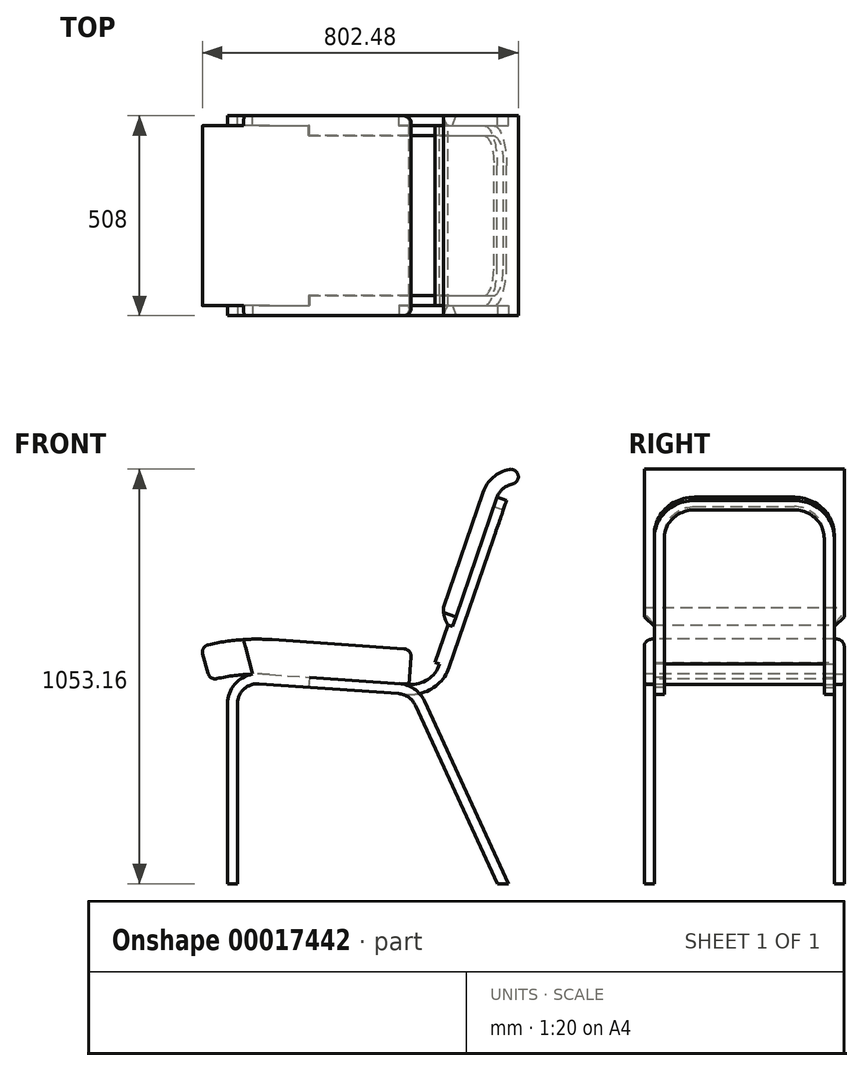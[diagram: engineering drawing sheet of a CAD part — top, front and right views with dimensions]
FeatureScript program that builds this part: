
annotation { "Feature Type Name" : "Feature", "Feature Type Description" : "" }
export const myFeature = defineFeature(function(context is Context, id is Id, definition is map)
    precondition{}
    {
        {
            var Q0;
            Q0=qCreatedBy(makeId("Front.planeOp"),FACE);
            cPlane(context, id + "F0", {"entities" : qUnion([Q0]), "cplaneType" : CPlaneType.OFFSET, "offset" : 254 * mm, "oppositeDirection" : true, "width" : 152.4 * mm, "height" : 152.4 * mm});
        }
        {
            var Q0;
            Q0=qCreatedBy(makeId("Front.planeOp"),FACE);
            var sketch = newSketch(context, id + "F1", { "sketchPlane" : qUnion([Q0])});
            skLineSegment(sketch, "E0", {"start": v(0, 0) * mm, "end": v(0, 457.2) * mm});
            skLineSegment(sketch, "E1", {"start": v(54.34, 507.88) * mm, "end": v(409.08, 483.07) * mm});
            skLineSegment(sketch, "E2", {"start": v(451.68, 453.63) * mm, "end": v(660.4, 0) * mm});
            skPoint(sketch, "E3.visualSharp", {"position": v(0, 511.68) * mm});
            skArc(sketch, "E3.filletArc", {"start": v(54.34, 507.88) * mm, "mid": v(16.15, 494.35) * mm, "end": v(0, 457.2) * mm});
            skPoint(sketch, "E4.visualSharp", {"position": v(439.1, 480.97) * mm});
            skArc(sketch, "E4.filletArc", {"start": v(451.68, 453.63) * mm, "mid": v(434.41, 474.19) * mm, "end": v(409.08, 483.07) * mm});
            skLineSegment(sketch, "E5.0", {"start": v(474.76, 464.25) * mm, "end": v(688.36, 0) * mm});
            skArc(sketch, "E5.1", {"start": v(474.76, 464.25) * mm, "mid": v(448.85, 495.08) * mm, "end": v(410.85, 508.4) * mm});
            skLineSegment(sketch, "E5.2", {"start": v(56.12, 533.21) * mm, "end": v(410.85, 508.4) * mm});
            skArc(sketch, "E5.3", {"start": v(56.12, 533.21) * mm, "mid": v(-1.17, 512.93) * mm, "end": v(-25.4, 457.2) * mm});
            skLineSegment(sketch, "E5.4", {"start": v(-25.4, 0) * mm, "end": v(-25.4, 457.2) * mm});
            skLineSegment(sketch, "E6", {"start": v(660.4, 0) * mm, "end": v(688.36, 0) * mm});
            skLineSegment(sketch, "E7", {"start": v(-25.4, 0) * mm, "end": v(0, 0) * mm});
            skSolve(sketch);
        }
        {
            var Q0;
            Q0=makeQuery(id+"F1.imprint","IMPRINT",FACE,{"disambiguationData":[TD([[makeQuery(id+"F1.imprint","IMPRINT",EDGE,{"derivedFrom":sQuery(id+"F1.wireOp",EDGE,"E0")}),1.0]])]});
            extrude(context, id + "F2", {"entities" : qUnion([Q0]), "oppositeDirection" : true, "depth" : 25.4 * mm});
        }
        {
            var Q0;
            Q0=makeQuery(id+"F2.opExtrude","CAP_FACE",FACE,{"disambiguationData":[OSD([sQuery(id+"F1.wireOp",EDGE,"E0"),sQuery(id+"F1.wireOp",EDGE,"E1"),sQuery(id+"F1.wireOp",EDGE,"E2"),sQuery(id+"F1.wireOp",EDGE,"E3.filletArc"),sQuery(id+"F1.wireOp",EDGE,"E4.filletArc"),sQuery(id+"F1.wireOp",EDGE,"E5.0"),sQuery(id+"F1.wireOp",EDGE,"E5.1"),sQuery(id+"F1.wireOp",EDGE,"E5.2"),sQuery(id+"F1.wireOp",EDGE,"E5.3"),sQuery(id+"F1.wireOp",EDGE,"E5.4"),sQuery(id+"F1.wireOp",EDGE,"E6"),sQuery(id+"F1.wireOp",EDGE,"E7")])],"isStart":false});
            var sketch = newSketch(context, id + "F3", { "sketchPlane" : qUnion([Q0])});
            skArc(sketch, "E8", {"start": v(-436.19, 506.64) * mm, "mid": v(-483.56, 519.1) * mm, "end": v(-513.55, 557.84) * mm});
            skArc(sketch, "E9.0", {"start": v(-434.42, 481.3) * mm, "mid": v(-497.58, 497.93) * mm, "end": v(-537.57, 549.57) * mm});
            skLineSegment(sketch, "E10", {"start": v(-513.55, 557.84) * mm, "end": v(-537.57, 549.57) * mm});
            skLineSegment(sketch, "E11", {"start": v(-436.19, 506.64) * mm, "end": v(-182.8, 524.36) * mm});
            skLineSegment(sketch, "E12", {"start": v(-182.8, 524.36) * mm, "end": v(-181.03, 499.02) * mm});
            skLineSegment(sketch, "E13", {"start": v(-181.03, 499.02) * mm, "end": v(-434.42, 481.3) * mm});
            skLineSegment(sketch, "E14", {"start": v(-441.5, 582.65) * mm, "end": v(-434.42, 481.3) * mm, "construction": true});
            skLineSegment(sketch, "E15", {"start": v(-441.5, 582.65) * mm, "end": v(-537.57, 549.57) * mm, "construction": true});
            skLineSegment(sketch, "E16.0", {"start": v(-56.12, 533.21) * mm, "end": v(-410.85, 508.4) * mm, "construction": true});
            skSolve(sketch);
        }
        {
            var Q0;
            Q0 = qSketchRegion(id + "F3", true);
            extrude(context, id + "F4", {"entities" : qUnion([Q0]), "operationType" : NewBodyOperationType.ADD, "depth" : 25.4 * mm});
        }
        {
            var Q0;
            Q0=makeQuery(id+"F4.opExtrude","SWEPT_EDGE",EDGE,{"disambiguationData":[OSD([sQuery(id+"F3.wireOp",EDGE,"E9.0"),sQuery(id+"F3.wireOp",EDGE,"E10")])]});
            cPlane(context, id + "F5", {"entities" : qUnion([Q0]), "cplaneType" : CPlaneType.LINE_ANGLE, "offset" : 152.4 * mm, "angle" : 71 * degree, "width" : 152.4 * mm, "height" : 152.4 * mm});
        }
        {
            var Q0;
            Q0=qCreatedBy(id+"F5.planeOp",FACE);
            var sketch = newSketch(context, id + "F6", { "sketchPlane" : qUnion([Q0])});
            skLineSegment(sketch, "E17", {"start": v(25.4, 694.65) * mm, "end": v(25.4, 1041.73) * mm});
            skLineSegment(sketch, "E18", {"start": v(127, 1143.33) * mm, "end": v(254, 1143.33) * mm});
            skPoint(sketch, "E19.visualSharp", {"position": v(25.4, 1143.33) * mm});
            skArc(sketch, "E19.filletArc", {"start": v(127, 1143.33) * mm, "mid": v(55.16, 1113.57) * mm, "end": v(25.4, 1041.73) * mm});
            skSolve(sketch);
        }
        {
            var Q0;
            Q0=makeQuery(id+"F4.opExtrude","SWEPT_FACE",FACE,{"disambiguationData":[OSD([sQuery(id+"F3.wireOp",EDGE,"E10")])]});
            var Q1;
            Q1 = qConstructionFilter(qBodyType(qCreatedBy(id + "F6" ,EDGE), BodyType.WIRE), ConstructionObject.NO);
            sweep(context, id + "F7", {"operationType" : NewBodyOperationType.ADD, "profiles" : qUnion([Q0]), "path" : qUnion([Q1])});
        }
        {
            var Q0;
            Q0=makeQuery(id+"F4.opExtrude","SWEPT_EDGE",EDGE,{"disambiguationData":[OSD([sQuery(id+"F3.wireOp",EDGE,"E8"),sQuery(id+"F3.wireOp",EDGE,"E11")])]});
            cPlane(context, id + "F8", {"entities" : qUnion([Q0]), "cplaneType" : CPlaneType.LINE_ANGLE, "offset" : 152.4 * mm, "angle" : 86 * degree, "width" : 152.4 * mm, "height" : 152.4 * mm});
        }
        {
            var Q0;
            Q0=qCreatedBy(id+"F8.planeOp",FACE);
            var sketch = newSketch(context, id + "F9", { "sketchPlane" : qUnion([Q0])});
            skLineSegment(sketch, "E20.bottom", {"start": v(0, 535.83) * mm, "end": v(254, 535.83) * mm});
            skLineSegment(sketch, "E20.top", {"start": v(0, 624.73) * mm, "end": v(254, 624.73) * mm});
            skLineSegment(sketch, "E20.left", {"start": v(0, 535.83) * mm, "end": v(0, 624.73) * mm});
            skLineSegment(sketch, "E20.right", {"start": v(254, 535.83) * mm, "end": v(254, 624.73) * mm});
            skSolve(sketch);
        }
        {
            var Q0;
            Q0=qCreatedBy(makeId("Front.planeOp"),FACE);
            var sketch = newSketch(context, id + "F10", { "sketchPlane" : qUnion([Q0])});
            skLineSegment(sketch, "E21", {"start": v(436.19, 506.64) * mm, "end": v(81.45, 531.44) * mm});
            skArc(sketch, "E22", {"start": v(81.45, 531.44) * mm, "mid": v(5, 530.38) * mm, "end": v(-70.22, 516.59) * mm});
            skSolve(sketch);
        }
        {
            var Q0;
            Q0 = qSketchRegion(id + "F9", true);
            var Q1;
            Q1 = qConstructionFilter(qBodyType(qCreatedBy(id + "F10" ,EDGE), BodyType.WIRE), ConstructionObject.NO);
            sweep(context, id + "F11", {"operationType" : NewBodyOperationType.ADD, "profiles" : qUnion([Q0]), "path" : qUnion([Q1])});
        }
        {
            var Q0;
            Q0=qCreatedBy(id+"F0.planeOp",FACE);
            var sketch = newSketch(context, id + "F12", { "sketchPlane" : qUnion([Q0])});
            skLineSegment(sketch, "E23.0", {"start": v(513.55, 557.84) * mm, "end": v(626.55, 886.02) * mm});
            skLineSegment(sketch, "E24", {"start": v(513.55, 557.84) * mm, "end": v(501.54, 561.98) * mm});
            skLineSegment(sketch, "E25", {"start": v(501.54, 561.98) * mm, "end": v(534.62, 658.04) * mm});
            skLineSegment(sketch, "E26", {"start": v(523, 702.34) * mm, "end": v(623.6, 994.49) * mm});
            skLineSegment(sketch, "E27.0", {"start": v(626.55, 886.02) * mm, "end": v(659.63, 982.08) * mm});
            skLineSegment(sketch, "E28", {"start": v(513.55, 557.84) * mm, "end": v(659.63, 982.08) * mm, "construction": true});
            skArc(sketch, "E29", {"start": v(659.63, 982.08) * mm, "mid": v(674.33, 1003.88) * mm, "end": v(697.97, 1015.41) * mm});
            skArc(sketch, "E30.0", {"start": v(623.6, 994.49) * mm, "mid": v(649.34, 1032.64) * mm, "end": v(690.7, 1052.81) * mm});
            skLineSegment(sketch, "E31", {"start": v(713.02, 1037.83) * mm, "end": v(713.02, 1037.83) * mm});
            skPoint(sketch, "E32.visualSharp", {"position": v(717.48, 1015.39) * mm});
            skArc(sketch, "E32.filletArc", {"start": v(697.97, 1015.41) * mm, "mid": v(710.15, 1023.5) * mm, "end": v(713.02, 1037.83) * mm});
            skPoint(sketch, "E33.visualSharp", {"position": v(709.71, 1054.42) * mm});
            skArc(sketch, "E33.filletArc", {"start": v(713.02, 1037.83) * mm, "mid": v(704.95, 1049.93) * mm, "end": v(690.7, 1052.81) * mm});
            skLineSegment(sketch, "E34", {"start": v(697.97, 1015.41) * mm, "end": v(707.66, 965.54) * mm, "construction": true});
            skLineSegment(sketch, "E35", {"start": v(659.63, 982.08) * mm, "end": v(707.66, 965.54) * mm, "construction": true});
            skArc(sketch, "E36", {"start": v(523, 702.34) * mm, "mid": v(525.4, 679.3) * mm, "end": v(534.62, 658.04) * mm});
            skSolve(sketch);
        }
        {
            var Q0;
            Q0 = qSketchRegion(id + "F12", true);
            var Q1;
            Q1=makeQuery(id+"F11.boolean.opBoolean","MERGE",FACE,{"derivedFrom":[makeQuery(id+"F2.opExtrude","CAP_FACE",FACE,{"disambiguationData":[OSD([sQuery(id+"F1.wireOp",EDGE,"E0"),sQuery(id+"F1.wireOp",EDGE,"E1"),sQuery(id+"F1.wireOp",EDGE,"E2"),sQuery(id+"F1.wireOp",EDGE,"E3.filletArc"),sQuery(id+"F1.wireOp",EDGE,"E4.filletArc"),sQuery(id+"F1.wireOp",EDGE,"E5.0"),sQuery(id+"F1.wireOp",EDGE,"E5.1"),sQuery(id+"F1.wireOp",EDGE,"E5.2"),sQuery(id+"F1.wireOp",EDGE,"E5.3"),sQuery(id+"F1.wireOp",EDGE,"E5.4"),sQuery(id+"F1.wireOp",EDGE,"E6"),sQuery(id+"F1.wireOp",EDGE,"E7")])],"isStart":true}),makeQuery(id+"F11.opSweep","SWEPT_FACE",FACE,{"disambiguationData":[OSD([sQuery(id+"F9.wireOp",EDGE,"E20.left"),sQuery(id+"F10.wireOp",EDGE,"E21")])]})]});
            extrude(context, id + "F13", {"entities" : qUnion([Q0]), "operationType" : NewBodyOperationType.ADD, "endBound" : BoundingType.UP_TO_SURFACE, "endBoundEntityFace" : qUnion([Q1]), "depth" : 30.48 * mm});
        }
        {
            var Q0;
            Q0=makeQuery(id+"F13.boolean.opBoolean","SPLIT",FACE,{"disambiguationData":[TD([makeQuery(id+"F13.opExtrude","SWEPT_FACE",FACE,{"disambiguationData":[OSD([sQuery(id+"F12.wireOp",EDGE,"E29")])]})])],"derivedFrom":makeQuery(id+"F13.opExtrude","SWEPT_FACE",FACE,{"disambiguationData":[OSD([sQuery(id+"F12.wireOp",EDGE,"E23.0"),sQuery(id+"F12.wireOp",EDGE,"E27.0")])]})});
            var sketch = newSketch(context, id + "F14", { "sketchPlane" : qUnion([Q0])});
            skLineSegment(sketch, "E37", {"start": v(25.4, 694.65) * mm, "end": v(25.4, 796.25) * mm});
            skLineSegment(sketch, "E38", {"start": v(25.4, 796.25) * mm, "end": v(0, 821.65) * mm});
            skLineSegment(sketch, "E39", {"start": v(0, 821.65) * mm, "end": v(0, 694.65) * mm});
            skLineSegment(sketch, "E40", {"start": v(0, 694.65) * mm, "end": v(25.4, 694.65) * mm});
            skSolve(sketch);
        }
        {
            var Q0;
            Q0 = qSketchRegion(id + "F14", true);
            extrude(context, id + "F15", {"entities" : qUnion([Q0]), "operationType" : NewBodyOperationType.REMOVE, "endBound" : BoundingType.UP_TO_NEXT, "oppositeDirection" : true, "depth" : 30.48 * mm});
        }
        {
            var Q0;
            Q0=makeQuery(id+"F11.boolean.opBoolean","MERGE",FACE,{"derivedFrom":[makeQuery(id+"F2.opExtrude","CAP_FACE",FACE,{"disambiguationData":[OSD([sQuery(id+"F1.wireOp",EDGE,"E0"),sQuery(id+"F1.wireOp",EDGE,"E1"),sQuery(id+"F1.wireOp",EDGE,"E2"),sQuery(id+"F1.wireOp",EDGE,"E3.filletArc"),sQuery(id+"F1.wireOp",EDGE,"E4.filletArc"),sQuery(id+"F1.wireOp",EDGE,"E5.0"),sQuery(id+"F1.wireOp",EDGE,"E5.1"),sQuery(id+"F1.wireOp",EDGE,"E5.2"),sQuery(id+"F1.wireOp",EDGE,"E5.3"),sQuery(id+"F1.wireOp",EDGE,"E5.4"),sQuery(id+"F1.wireOp",EDGE,"E6"),sQuery(id+"F1.wireOp",EDGE,"E7")])],"isStart":true}),makeQuery(id+"F11.opSweep","SWEPT_FACE",FACE,{"disambiguationData":[OSD([sQuery(id+"F9.wireOp",EDGE,"E20.left"),sQuery(id+"F10.wireOp",EDGE,"E21")])]})]});
            var sketch = newSketch(context, id + "F16", { "sketchPlane" : qUnion([Q0])});
            skArc(sketch, "E41.0", {"start": v(14.79, 620.35) * mm, "mid": v(-39.81, 614.1) * mm, "end": v(-93.51, 602.38) * mm});
            skLineSegment(sketch, "E41.1", {"start": v(-93.51, 602.38) * mm, "end": v(-70.22, 516.59) * mm});
            skArc(sketch, "E41.2", {"start": v(38.66, 532.43) * mm, "mid": v(-16.26, 527.8) * mm, "end": v(-70.22, 516.59) * mm});
            skLineSegment(sketch, "E42", {"start": v(38.66, 532.43) * mm, "end": v(14.79, 620.35) * mm});
            skPoint(sketch, "E43.orphan", {"position": v(87.65, 620.13) * mm});
            skSolve(sketch);
        }
        {
            var Q0;
            Q0 = qSketchRegion(id + "F16", true);
            extrude(context, id + "F17", {"entities" : qUnion([Q0]), "operationType" : NewBodyOperationType.REMOVE, "oppositeDirection" : true, "depth" : 25.4 * mm});
        }
        {
            var Q0;
            Q0=makeQuery(id+"F2.opExtrude","SWEPT_BODY",BODY,{"disambiguationData":[OSD([sQuery(id+"F1.wireOp",EDGE,"E0"),sQuery(id+"F1.wireOp",EDGE,"E1"),sQuery(id+"F1.wireOp",EDGE,"E2"),sQuery(id+"F1.wireOp",EDGE,"E3.filletArc"),sQuery(id+"F1.wireOp",EDGE,"E4.filletArc"),sQuery(id+"F1.wireOp",EDGE,"E5.0"),sQuery(id+"F1.wireOp",EDGE,"E5.1"),sQuery(id+"F1.wireOp",EDGE,"E5.2"),sQuery(id+"F1.wireOp",EDGE,"E5.3"),sQuery(id+"F1.wireOp",EDGE,"E5.4"),sQuery(id+"F1.wireOp",EDGE,"E6"),sQuery(id+"F1.wireOp",EDGE,"E7")])]});
            var Q1;
            Q1=qCreatedBy(id+"F0.planeOp",FACE);
            mirror(context, id + "F18", {"operationType" : NewBodyOperationType.ADD, "entities" : qUnion([Q0]), "mirrorPlane" : qUnion([Q1])});
        }
        {
            var Q0;
            {var subQ0=makeQuery(id+"F11.opSweep","CAP_EDGE",EDGE,{"disambiguationData":[OSD([sQuery(id+"F9.wireOp",EDGE,"E20.top"),sQuery(id+"F10.wireOp",VERTEX,"E22.end")])],"isStart":false});Q0=makeQuery(id+"F18.boolean.opBoolean","MERGE",EDGE,{"derivedFrom":[subQ0,makeQuery(id+"F18.opPattern","COPY",EDGE,{"derivedFrom":subQ0,"instanceName":"1"})]});}
            var Q1;
            Q1=makeQuery(id+"F17.boolean.opBoolean","COPY",EDGE,{"derivedFrom":makeQuery(id+"F17.opExtrude","CAP_EDGE",EDGE,{"disambiguationData":[OSD([sQuery(id+"F16.wireOp",EDGE,"E41.0")])],"isStart":false})});
            var Q2;
            Q2=makeQuery(id+"F17.boolean.opBoolean","COPY",EDGE,{"derivedFrom":makeQuery(id+"F17.opExtrude","SWEPT_EDGE",EDGE,{"disambiguationData":[OSD([sQuery(id+"F9.wireOp",EDGE,"E20.top"),sQuery(id+"F9.wireOp",EDGE,"E20.left"),sQuery(id+"F10.wireOp",EDGE,"E22"),sQuery(id+"F16.wireOp",EDGE,"E41.0"),sQuery(id+"F16.wireOp",EDGE,"E42")])]})});
            var Q3;
            {var subQ0=makeQuery(id+"F11.opSweep","CAP_EDGE",EDGE,{"disambiguationData":[OSD([sQuery(id+"F9.wireOp",EDGE,"E20.bottom"),sQuery(id+"F10.wireOp",VERTEX,"E22.end")])],"isStart":false});Q3=makeQuery(id+"F18.boolean.opBoolean","MERGE",EDGE,{"derivedFrom":[subQ0,makeQuery(id+"F18.opPattern","COPY",EDGE,{"derivedFrom":subQ0,"instanceName":"1"})]});}
            var Q4;
            Q4=makeQuery(id+"F17.boolean.opBoolean","COPY",EDGE,{"derivedFrom":makeQuery(id+"F17.opExtrude","CAP_EDGE",EDGE,{"disambiguationData":[OSD([sQuery(id+"F16.wireOp",EDGE,"E41.2")])],"isStart":false})});
            var Q5;
            Q5=makeQuery(id+"F17.boolean.opBoolean","COPY",EDGE,{"derivedFrom":makeQuery(id+"F17.opExtrude","CAP_EDGE",EDGE,{"disambiguationData":[OSD([sQuery(id+"F16.wireOp",EDGE,"E41.1")])],"isStart":false})});
            var Q6;
            Q6=makeQuery(id+"F17.boolean.opBoolean","COPY",EDGE,{"derivedFrom":makeQuery(id+"F17.opExtrude","CAP_EDGE",EDGE,{"disambiguationData":[OSD([sQuery(id+"F16.wireOp",EDGE,"E42")])],"isStart":true})});
            var Q7;
            Q7=makeQuery(id+"F11.opSweep","SWEPT_EDGE",EDGE,{"disambiguationData":[OSD([sQuery(id+"F9.wireOp",EDGE,"E20.top"),sQuery(id+"F9.wireOp",EDGE,"E20.left"),sQuery(id+"F10.wireOp",EDGE,"E22")])]});
            var Q8;
            Q8=makeQuery(id+"F11.opSweep","SWEPT_EDGE",EDGE,{"disambiguationData":[OSD([sQuery(id+"F9.wireOp",EDGE,"E20.top"),sQuery(id+"F9.wireOp",EDGE,"E20.left"),sQuery(id+"F10.wireOp",EDGE,"E21")])]});
            var Q9;
            {var subQ0=makeQuery(id+"F11.opSweep","CAP_EDGE",EDGE,{"disambiguationData":[OSD([sQuery(id+"F9.wireOp",EDGE,"E20.top"),sQuery(id+"F10.wireOp",VERTEX,"E21.start")])],"isStart":true});Q9=makeQuery(id+"F18.boolean.opBoolean","MERGE",EDGE,{"derivedFrom":[subQ0,makeQuery(id+"F18.opPattern","COPY",EDGE,{"derivedFrom":subQ0,"instanceName":"1"})]});}
            var Q10;
            Q10=makeQuery(id+"F11.opSweep","CAP_EDGE",EDGE,{"disambiguationData":[OSD([sQuery(id+"F9.wireOp",EDGE,"E20.left"),sQuery(id+"F10.wireOp",VERTEX,"E21.start")])],"isStart":true});
            var Q11;
            Q11=makeQuery(id+"F18.opPattern","COPY",EDGE,{"derivedFrom":makeQuery(id+"F17.boolean.opBoolean","COPY",EDGE,{"derivedFrom":makeQuery(id+"F17.opExtrude","CAP_EDGE",EDGE,{"disambiguationData":[OSD([sQuery(id+"F16.wireOp",EDGE,"E41.0")])],"isStart":false})}),"instanceName":"1"});
            var Q12;
            Q12=makeQuery(id+"F18.opPattern","COPY",EDGE,{"derivedFrom":makeQuery(id+"F11.opSweep","SWEPT_EDGE",EDGE,{"disambiguationData":[OSD([sQuery(id+"F9.wireOp",EDGE,"E20.top"),sQuery(id+"F9.wireOp",EDGE,"E20.left"),sQuery(id+"F10.wireOp",EDGE,"E22")])]}),"instanceName":"1"});
            var Q13;
            Q13=makeQuery(id+"F18.opPattern","COPY",EDGE,{"derivedFrom":makeQuery(id+"F11.opSweep","SWEPT_EDGE",EDGE,{"disambiguationData":[OSD([sQuery(id+"F9.wireOp",EDGE,"E20.top"),sQuery(id+"F9.wireOp",EDGE,"E20.left"),sQuery(id+"F10.wireOp",EDGE,"E21")])]}),"instanceName":"1"});
            var Q14;
            Q14=makeQuery(id+"F18.opPattern","COPY",EDGE,{"derivedFrom":makeQuery(id+"F17.boolean.opBoolean","COPY",EDGE,{"derivedFrom":makeQuery(id+"F17.opExtrude","SWEPT_EDGE",EDGE,{"disambiguationData":[OSD([sQuery(id+"F9.wireOp",EDGE,"E20.top"),sQuery(id+"F9.wireOp",EDGE,"E20.left"),sQuery(id+"F10.wireOp",EDGE,"E22"),sQuery(id+"F16.wireOp",EDGE,"E41.0"),sQuery(id+"F16.wireOp",EDGE,"E42")])]})}),"instanceName":"1"});
            var Q15;
            Q15=makeQuery(id+"F18.opPattern","COPY",EDGE,{"derivedFrom":makeQuery(id+"F17.boolean.opBoolean","COPY",EDGE,{"derivedFrom":makeQuery(id+"F17.opExtrude","CAP_EDGE",EDGE,{"disambiguationData":[OSD([sQuery(id+"F16.wireOp",EDGE,"E42")])],"isStart":true})}),"instanceName":"1"});
            var Q16;
            Q16=makeQuery(id+"F18.opPattern","COPY",EDGE,{"derivedFrom":makeQuery(id+"F17.boolean.opBoolean","COPY",EDGE,{"derivedFrom":makeQuery(id+"F17.opExtrude","CAP_EDGE",EDGE,{"disambiguationData":[OSD([sQuery(id+"F16.wireOp",EDGE,"E41.1")])],"isStart":false})}),"instanceName":"1"});
            var Q17;
            Q17=makeQuery(id+"F18.opPattern","COPY",EDGE,{"derivedFrom":makeQuery(id+"F17.boolean.opBoolean","COPY",EDGE,{"derivedFrom":makeQuery(id+"F17.opExtrude","CAP_EDGE",EDGE,{"disambiguationData":[OSD([sQuery(id+"F16.wireOp",EDGE,"E41.2")])],"isStart":false})}),"instanceName":"1"});
            var Q18;
            Q18=makeQuery(id+"F18.opPattern","COPY",EDGE,{"derivedFrom":makeQuery(id+"F11.opSweep","CAP_EDGE",EDGE,{"disambiguationData":[OSD([sQuery(id+"F9.wireOp",EDGE,"E20.left"),sQuery(id+"F10.wireOp",VERTEX,"E21.start")])],"isStart":true}),"instanceName":"1"});
            var Q19;
            Q19=makeQuery(id+"F18.opPattern","COPY",EDGE,{"derivedFrom":makeQuery(id+"F13.opExtrude","TWEAK_EDGE",EDGE,{"derivedFrom":[makeQuery(id+"F11.boolean.opBoolean","MERGE",FACE,{"derivedFrom":[makeQuery(id+"F2.opExtrude","CAP_FACE",FACE,{"disambiguationData":[OSD([sQuery(id+"F1.wireOp",EDGE,"E0"),sQuery(id+"F1.wireOp",EDGE,"E1"),sQuery(id+"F1.wireOp",EDGE,"E2"),sQuery(id+"F1.wireOp",EDGE,"E3.filletArc"),sQuery(id+"F1.wireOp",EDGE,"E4.filletArc"),sQuery(id+"F1.wireOp",EDGE,"E5.0"),sQuery(id+"F1.wireOp",EDGE,"E5.1"),sQuery(id+"F1.wireOp",EDGE,"E5.2"),sQuery(id+"F1.wireOp",EDGE,"E5.3"),sQuery(id+"F1.wireOp",EDGE,"E5.4"),sQuery(id+"F1.wireOp",EDGE,"E6"),sQuery(id+"F1.wireOp",EDGE,"E7")])],"isStart":true}),makeQuery(id+"F11.opSweep","SWEPT_FACE",FACE,{"disambiguationData":[OSD([sQuery(id+"F9.wireOp",EDGE,"E20.left"),sQuery(id+"F10.wireOp",EDGE,"E21")])]})]}),makeQuery(id+"F12.imprint","IMPRINT",EDGE,{"derivedFrom":sQuery(id+"F12.wireOp",EDGE,"E26")})]}),"instanceName":"1"});
            var Q20;
            Q20=makeQuery(id+"F18.opPattern","COPY",EDGE,{"derivedFrom":makeQuery(id+"F13.opExtrude","TWEAK_EDGE",EDGE,{"derivedFrom":[makeQuery(id+"F11.boolean.opBoolean","MERGE",FACE,{"derivedFrom":[makeQuery(id+"F2.opExtrude","CAP_FACE",FACE,{"disambiguationData":[OSD([sQuery(id+"F1.wireOp",EDGE,"E0"),sQuery(id+"F1.wireOp",EDGE,"E1"),sQuery(id+"F1.wireOp",EDGE,"E2"),sQuery(id+"F1.wireOp",EDGE,"E3.filletArc"),sQuery(id+"F1.wireOp",EDGE,"E4.filletArc"),sQuery(id+"F1.wireOp",EDGE,"E5.0"),sQuery(id+"F1.wireOp",EDGE,"E5.1"),sQuery(id+"F1.wireOp",EDGE,"E5.2"),sQuery(id+"F1.wireOp",EDGE,"E5.3"),sQuery(id+"F1.wireOp",EDGE,"E5.4"),sQuery(id+"F1.wireOp",EDGE,"E6"),sQuery(id+"F1.wireOp",EDGE,"E7")])],"isStart":true}),makeQuery(id+"F11.opSweep","SWEPT_FACE",FACE,{"disambiguationData":[OSD([sQuery(id+"F9.wireOp",EDGE,"E20.left"),sQuery(id+"F10.wireOp",EDGE,"E21")])]})]}),makeQuery(id+"F12.imprint","IMPRINT",EDGE,{"derivedFrom":sQuery(id+"F12.wireOp",EDGE,"E30.0")})]}),"instanceName":"1"});
            var Q21;
            Q21=makeQuery(id+"F18.opPattern","COPY",EDGE,{"derivedFrom":makeQuery(id+"F13.opExtrude","TWEAK_EDGE",EDGE,{"derivedFrom":[makeQuery(id+"F11.boolean.opBoolean","MERGE",FACE,{"derivedFrom":[makeQuery(id+"F2.opExtrude","CAP_FACE",FACE,{"disambiguationData":[OSD([sQuery(id+"F1.wireOp",EDGE,"E0"),sQuery(id+"F1.wireOp",EDGE,"E1"),sQuery(id+"F1.wireOp",EDGE,"E2"),sQuery(id+"F1.wireOp",EDGE,"E3.filletArc"),sQuery(id+"F1.wireOp",EDGE,"E4.filletArc"),sQuery(id+"F1.wireOp",EDGE,"E5.0"),sQuery(id+"F1.wireOp",EDGE,"E5.1"),sQuery(id+"F1.wireOp",EDGE,"E5.2"),sQuery(id+"F1.wireOp",EDGE,"E5.3"),sQuery(id+"F1.wireOp",EDGE,"E5.4"),sQuery(id+"F1.wireOp",EDGE,"E6"),sQuery(id+"F1.wireOp",EDGE,"E7")])],"isStart":true}),makeQuery(id+"F11.opSweep","SWEPT_FACE",FACE,{"disambiguationData":[OSD([sQuery(id+"F9.wireOp",EDGE,"E20.left"),sQuery(id+"F10.wireOp",EDGE,"E21")])]})]}),makeQuery(id+"F12.imprint","IMPRINT",EDGE,{"derivedFrom":sQuery(id+"F12.wireOp",EDGE,"E29")})]}),"instanceName":"1"});
            var Q22;
            Q22=makeQuery(id+"F13.opExtrude","TWEAK_EDGE",EDGE,{"derivedFrom":[makeQuery(id+"F11.boolean.opBoolean","MERGE",FACE,{"derivedFrom":[makeQuery(id+"F2.opExtrude","CAP_FACE",FACE,{"disambiguationData":[OSD([sQuery(id+"F1.wireOp",EDGE,"E0"),sQuery(id+"F1.wireOp",EDGE,"E1"),sQuery(id+"F1.wireOp",EDGE,"E2"),sQuery(id+"F1.wireOp",EDGE,"E3.filletArc"),sQuery(id+"F1.wireOp",EDGE,"E4.filletArc"),sQuery(id+"F1.wireOp",EDGE,"E5.0"),sQuery(id+"F1.wireOp",EDGE,"E5.1"),sQuery(id+"F1.wireOp",EDGE,"E5.2"),sQuery(id+"F1.wireOp",EDGE,"E5.3"),sQuery(id+"F1.wireOp",EDGE,"E5.4"),sQuery(id+"F1.wireOp",EDGE,"E6"),sQuery(id+"F1.wireOp",EDGE,"E7")])],"isStart":true}),makeQuery(id+"F11.opSweep","SWEPT_FACE",FACE,{"disambiguationData":[OSD([sQuery(id+"F9.wireOp",EDGE,"E20.left"),sQuery(id+"F10.wireOp",EDGE,"E21")])]})]}),makeQuery(id+"F12.imprint","IMPRINT",EDGE,{"derivedFrom":sQuery(id+"F12.wireOp",EDGE,"E30.0")})]});
            var Q23;
            Q23=makeQuery(id+"F13.opExtrude","TWEAK_EDGE",EDGE,{"derivedFrom":[makeQuery(id+"F11.boolean.opBoolean","MERGE",FACE,{"derivedFrom":[makeQuery(id+"F2.opExtrude","CAP_FACE",FACE,{"disambiguationData":[OSD([sQuery(id+"F1.wireOp",EDGE,"E0"),sQuery(id+"F1.wireOp",EDGE,"E1"),sQuery(id+"F1.wireOp",EDGE,"E2"),sQuery(id+"F1.wireOp",EDGE,"E3.filletArc"),sQuery(id+"F1.wireOp",EDGE,"E4.filletArc"),sQuery(id+"F1.wireOp",EDGE,"E5.0"),sQuery(id+"F1.wireOp",EDGE,"E5.1"),sQuery(id+"F1.wireOp",EDGE,"E5.2"),sQuery(id+"F1.wireOp",EDGE,"E5.3"),sQuery(id+"F1.wireOp",EDGE,"E5.4"),sQuery(id+"F1.wireOp",EDGE,"E6"),sQuery(id+"F1.wireOp",EDGE,"E7")])],"isStart":true}),makeQuery(id+"F11.opSweep","SWEPT_FACE",FACE,{"disambiguationData":[OSD([sQuery(id+"F9.wireOp",EDGE,"E20.left"),sQuery(id+"F10.wireOp",EDGE,"E21")])]})]}),makeQuery(id+"F12.imprint","IMPRINT",EDGE,{"derivedFrom":sQuery(id+"F12.wireOp",EDGE,"E26")})]});
            var Q24;
            Q24=makeQuery(id+"F13.opExtrude","TWEAK_EDGE",EDGE,{"derivedFrom":[makeQuery(id+"F11.boolean.opBoolean","MERGE",FACE,{"derivedFrom":[makeQuery(id+"F2.opExtrude","CAP_FACE",FACE,{"disambiguationData":[OSD([sQuery(id+"F1.wireOp",EDGE,"E0"),sQuery(id+"F1.wireOp",EDGE,"E1"),sQuery(id+"F1.wireOp",EDGE,"E2"),sQuery(id+"F1.wireOp",EDGE,"E3.filletArc"),sQuery(id+"F1.wireOp",EDGE,"E4.filletArc"),sQuery(id+"F1.wireOp",EDGE,"E5.0"),sQuery(id+"F1.wireOp",EDGE,"E5.1"),sQuery(id+"F1.wireOp",EDGE,"E5.2"),sQuery(id+"F1.wireOp",EDGE,"E5.3"),sQuery(id+"F1.wireOp",EDGE,"E5.4"),sQuery(id+"F1.wireOp",EDGE,"E6"),sQuery(id+"F1.wireOp",EDGE,"E7")])],"isStart":true}),makeQuery(id+"F11.opSweep","SWEPT_FACE",FACE,{"disambiguationData":[OSD([sQuery(id+"F9.wireOp",EDGE,"E20.left"),sQuery(id+"F10.wireOp",EDGE,"E21")])]})]}),makeQuery(id+"F12.imprint","IMPRINT",EDGE,{"derivedFrom":sQuery(id+"F12.wireOp",EDGE,"E29")})]});
            var Q25;
            Q25=makeQuery(id+"F13.opExtrude","TWEAK_EDGE",EDGE,{"derivedFrom":[makeQuery(id+"F11.boolean.opBoolean","MERGE",FACE,{"derivedFrom":[makeQuery(id+"F2.opExtrude","CAP_FACE",FACE,{"disambiguationData":[OSD([sQuery(id+"F1.wireOp",EDGE,"E0"),sQuery(id+"F1.wireOp",EDGE,"E1"),sQuery(id+"F1.wireOp",EDGE,"E2"),sQuery(id+"F1.wireOp",EDGE,"E3.filletArc"),sQuery(id+"F1.wireOp",EDGE,"E4.filletArc"),sQuery(id+"F1.wireOp",EDGE,"E5.0"),sQuery(id+"F1.wireOp",EDGE,"E5.1"),sQuery(id+"F1.wireOp",EDGE,"E5.2"),sQuery(id+"F1.wireOp",EDGE,"E5.3"),sQuery(id+"F1.wireOp",EDGE,"E5.4"),sQuery(id+"F1.wireOp",EDGE,"E6"),sQuery(id+"F1.wireOp",EDGE,"E7")])],"isStart":true}),makeQuery(id+"F11.opSweep","SWEPT_FACE",FACE,{"disambiguationData":[OSD([sQuery(id+"F9.wireOp",EDGE,"E20.left"),sQuery(id+"F10.wireOp",EDGE,"E21")])]})]}),makeQuery(id+"F12.imprint","IMPRINT",EDGE,{"derivedFrom":sQuery(id+"F12.wireOp",EDGE,"E23.0")}),makeQuery(id+"F12.imprint","IMPRINT",EDGE,{"derivedFrom":sQuery(id+"F12.wireOp",EDGE,"E27.0")})]});
            var Q26;
            Q26=makeQuery(id+"F18.opPattern","COPY",EDGE,{"derivedFrom":makeQuery(id+"F13.opExtrude","TWEAK_EDGE",EDGE,{"derivedFrom":[makeQuery(id+"F11.boolean.opBoolean","MERGE",FACE,{"derivedFrom":[makeQuery(id+"F2.opExtrude","CAP_FACE",FACE,{"disambiguationData":[OSD([sQuery(id+"F1.wireOp",EDGE,"E0"),sQuery(id+"F1.wireOp",EDGE,"E1"),sQuery(id+"F1.wireOp",EDGE,"E2"),sQuery(id+"F1.wireOp",EDGE,"E3.filletArc"),sQuery(id+"F1.wireOp",EDGE,"E4.filletArc"),sQuery(id+"F1.wireOp",EDGE,"E5.0"),sQuery(id+"F1.wireOp",EDGE,"E5.1"),sQuery(id+"F1.wireOp",EDGE,"E5.2"),sQuery(id+"F1.wireOp",EDGE,"E5.3"),sQuery(id+"F1.wireOp",EDGE,"E5.4"),sQuery(id+"F1.wireOp",EDGE,"E6"),sQuery(id+"F1.wireOp",EDGE,"E7")])],"isStart":true}),makeQuery(id+"F11.opSweep","SWEPT_FACE",FACE,{"disambiguationData":[OSD([sQuery(id+"F9.wireOp",EDGE,"E20.left"),sQuery(id+"F10.wireOp",EDGE,"E21")])]})]}),makeQuery(id+"F12.imprint","IMPRINT",EDGE,{"derivedFrom":sQuery(id+"F12.wireOp",EDGE,"E23.0")}),makeQuery(id+"F12.imprint","IMPRINT",EDGE,{"derivedFrom":sQuery(id+"F12.wireOp",EDGE,"E27.0")})]}),"instanceName":"1"});
            fillet(context, id + "F19", {"entities" : qUnion([Q0, Q1, Q2, Q3, Q4, Q5, Q6, Q7, Q8, Q9, Q10, Q11, Q12, Q13, Q14, Q15, Q16, Q17, Q18, Q19, Q20, Q21, Q22, Q23, Q24, Q25, Q26]), "radius" : 19.05 * mm, "allowEdgeOverflow" : false});
        }
    });
